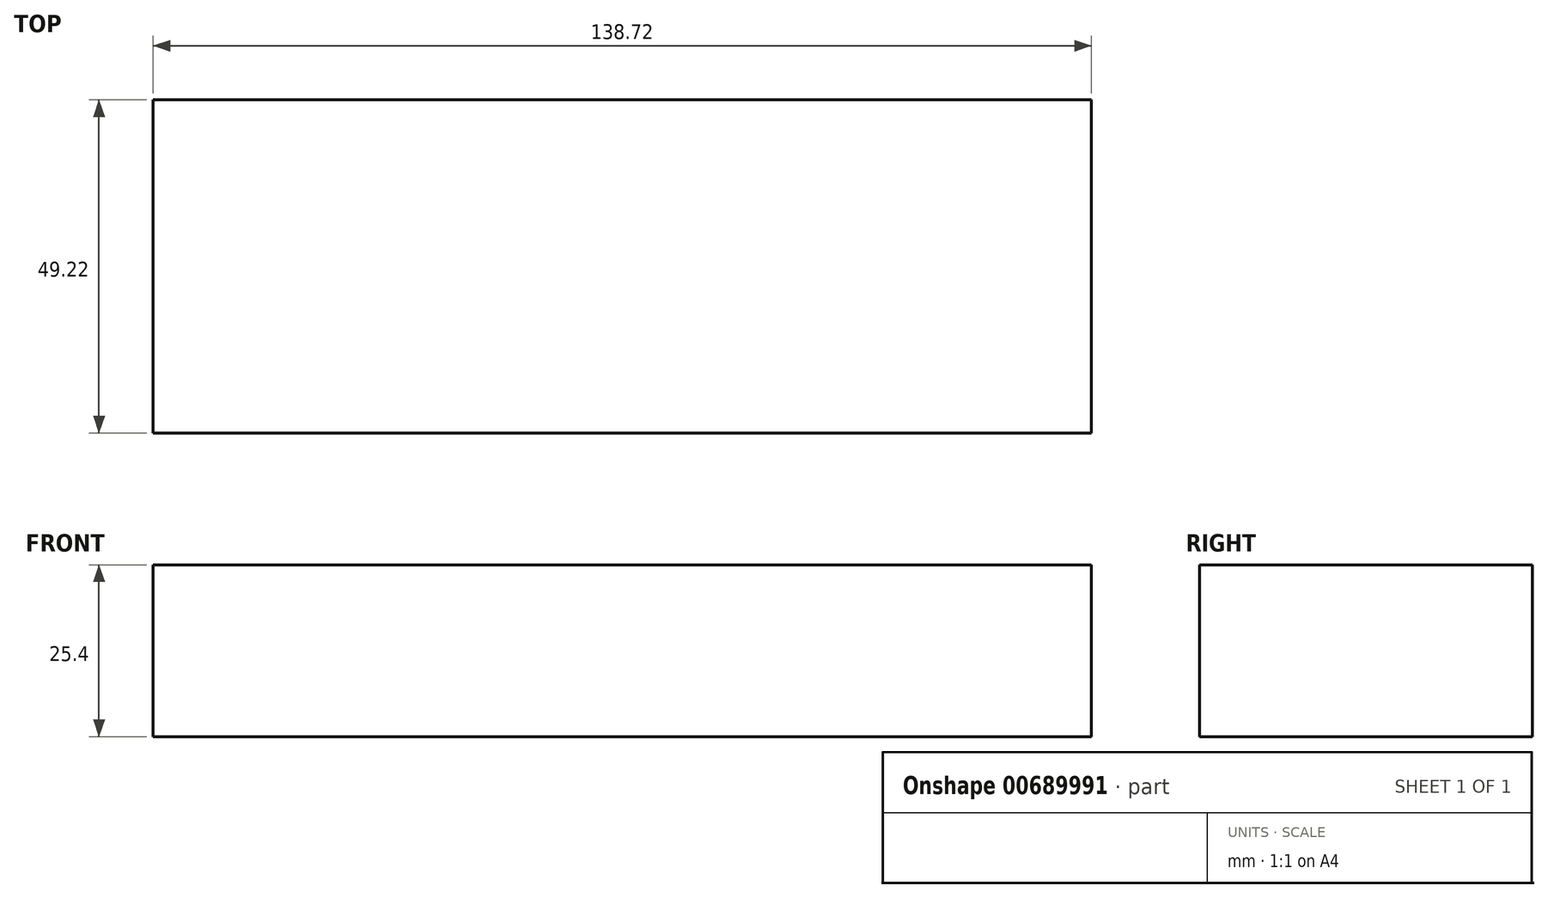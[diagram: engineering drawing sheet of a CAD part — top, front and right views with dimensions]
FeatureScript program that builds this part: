
annotation { "Feature Type Name" : "Feature", "Feature Type Description" : "" }
export const myFeature = defineFeature(function(context is Context, id is Id, definition is map)
    precondition{}
    {
        {
            var Q0;
            Q0=qCreatedBy(makeId("Top.planeOp"),FACE);
            var sketch = newSketch(context, id + "F0", { "sketchPlane" : qUnion([Q0])});
            skLineSegment(sketch, "E0.bottom", {"start": v(-113.23, 34.26) * mm, "end": v(25.5, 34.26) * mm});
            skLineSegment(sketch, "E0.top", {"start": v(-113.23, -14.96) * mm, "end": v(25.5, -14.96) * mm});
            skLineSegment(sketch, "E0.left", {"start": v(-113.23, 34.26) * mm, "end": v(-113.23, -14.96) * mm});
            skLineSegment(sketch, "E0.right", {"start": v(25.5, 34.26) * mm, "end": v(25.5, -14.96) * mm});
            skCircle(sketch, "E1", {"center": v(36.68, 30.53) * mm, "radius": 6.5 * mm});
            skCircle(sketch, "E2", {"center": v(37.42, 24.07) * mm, "radius": 39.89 * mm});
            skSolve(sketch);
        }
        {
            var Q0;
            {var subQ1=sQuery(id+"F0.wireOp",EDGE,"E0.top");Q0=makeQuery(id+"F0.imprint","IMPRINT",FACE,{"disambiguationData":[TD([[makeQuery(id+"F0.imprint","IMPRINT",EDGE,{"derivedFrom":subQ1}),1.0]])]});}
            var Q1;
            {var subQ0=sQuery(id+"F0.wireOp",EDGE,"E0.right");var subQ1=sQuery(id+"F0.wireOp",EDGE,"E0.bottom");var subQ2=makeQuery(id+"F0.imprint","INTERSECT",VERTEX,{"derivedFrom":[subQ1,subQ0]});Q1=makeQuery(id+"F0.imprint","IMPRINT",FACE,{"disambiguationData":[TD([[makeQuery(id+"F0.imprint","IMPRINT",EDGE,{"disambiguationData":[TD([[subQ2,1.0]])],"derivedFrom":subQ1}),-1.0]])]});}
            extrude(context, id + "F1", {"entities" : qUnion([Q0, Q1]), "depth" : 25.4 * mm, "offsetDistance" : 25.4 * mm});
        }
    });
